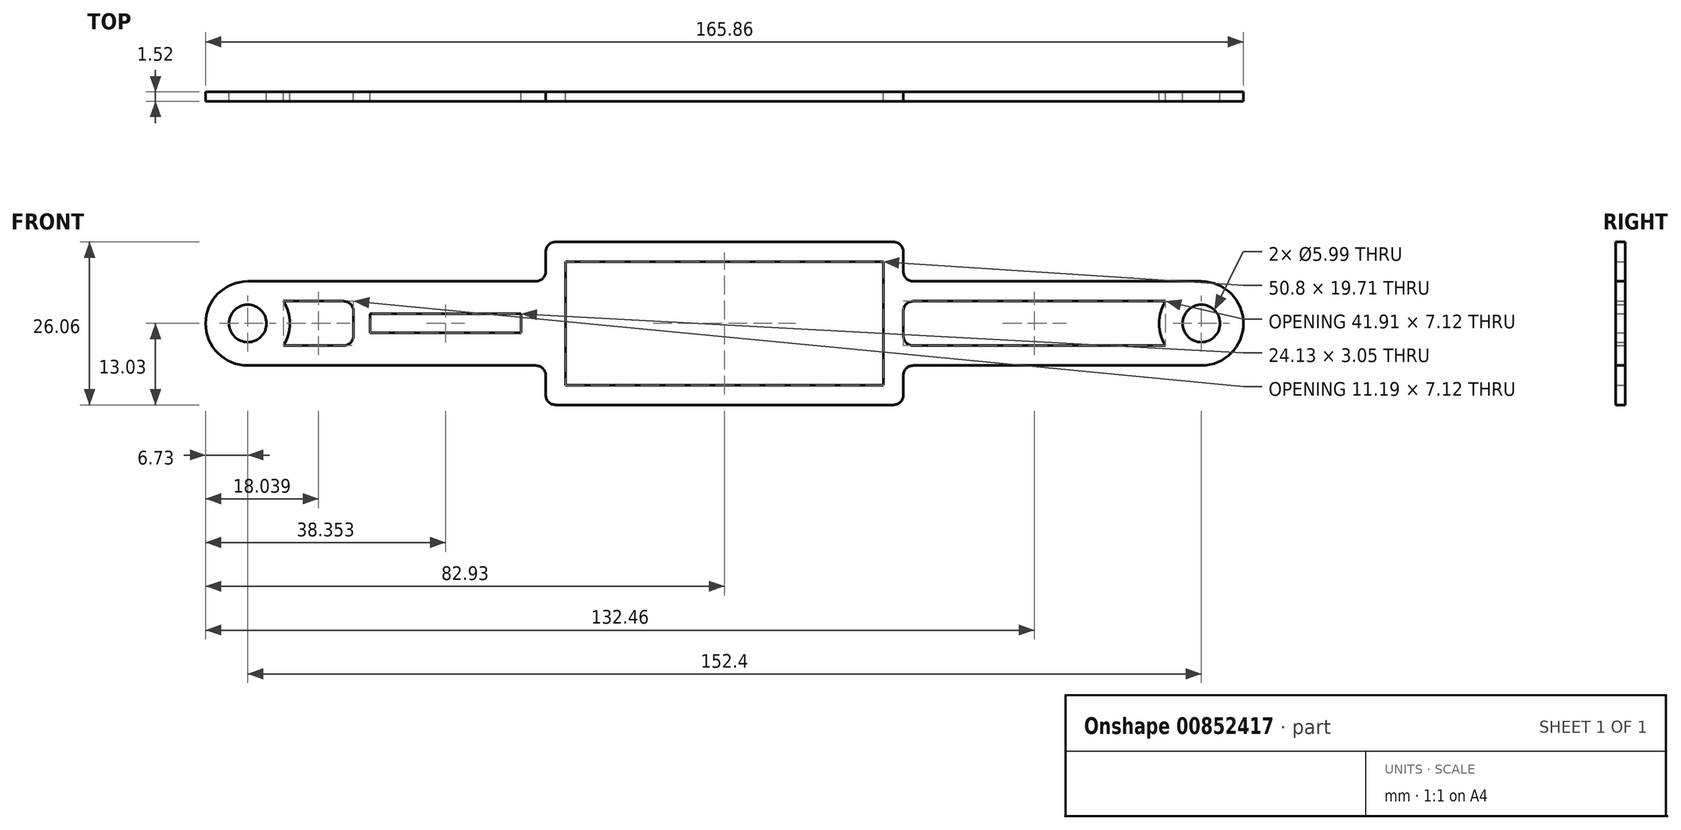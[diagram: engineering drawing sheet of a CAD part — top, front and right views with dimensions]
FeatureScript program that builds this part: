
annotation { "Feature Type Name" : "Feature", "Feature Type Description" : "" }
export const myFeature = defineFeature(function(context is Context, id is Id, definition is map)
    precondition{}
    {
        {
            var Q0;
            Q0=qCreatedBy(makeId("Front.planeOp"),FACE);
            var sketch = newSketch(context, id + "F0", { "sketchPlane" : qUnion([Q0])});
            skLineSegment(sketch, "E0.bottom", {"start": v(-76.2, -6.73) * mm, "end": v(-28.57, -6.73) * mm});
            skLineSegment(sketch, "E0.top", {"start": v(-76.2, 6.73) * mm, "end": v(-28.58, 6.73) * mm});
            skLineSegment(sketch, "E1.bottom", {"start": v(-25.4, 9.86) * mm, "end": v(25.4, 9.86) * mm});
            skLineSegment(sketch, "E1.top", {"start": v(-25.4, -9.86) * mm, "end": v(25.4, -9.86) * mm});
            skLineSegment(sketch, "E1.left", {"start": v(-25.4, 9.86) * mm, "end": v(-25.4, -9.86) * mm});
            skLineSegment(sketch, "E1.right", {"start": v(25.4, 9.86) * mm, "end": v(25.4, -9.86) * mm});
            skCircle(sketch, "E2", {"center": v(-76.2, 0) * mm, "radius": 3 * mm});
            skPoint(sketch, "E2.centerSnap0", {"position": v(-88.9, 0) * mm});
            skCircle(sketch, "E3", {"center": v(76.2, 0) * mm, "radius": 3 * mm});
            skLineSegment(sketch, "E4.bottom", {"start": v(-28.58, 13.03) * mm, "end": v(28.58, 13.03) * mm});
            skLineSegment(sketch, "E4.top", {"start": v(-28.58, -13.03) * mm, "end": v(28.58, -13.03) * mm});
            skLineSegment(sketch, "E4.left", {"start": v(-28.58, 13.03) * mm, "end": v(-28.58, 6.73) * mm});
            skLineSegment(sketch, "E4.right", {"start": v(28.58, 13.03) * mm, "end": v(28.58, 6.73) * mm});
            skArc(sketch, "E5", {"start": v(76.2, -6.73) * mm, "mid": v(82.93, 0) * mm, "end": v(76.2, 6.73) * mm});
            skArc(sketch, "E6", {"start": v(-76.2, 6.73) * mm, "mid": v(-82.93, 0) * mm, "end": v(-76.2, -6.73) * mm});
            skPoint(sketch, "E7.orphan", {"position": v(-88.9, 6.73) * mm});
            skPoint(sketch, "E8.orphan", {"position": v(-88.9, -6.73) * mm});
            skLineSegment(sketch, "E9.trimOffspring", {"start": v(-28.58, -6.73) * mm, "end": v(-28.58, -13.03) * mm});
            skLineSegment(sketch, "E10.trimOffspring", {"start": v(28.58, -6.73) * mm, "end": v(28.58, -13.03) * mm});
            skLineSegment(sketch, "E11.trimOffspring", {"start": v(28.58, 6.73) * mm, "end": v(76.2, 6.73) * mm});
            skLineSegment(sketch, "E12.trimOffspring", {"start": v(28.58, -6.73) * mm, "end": v(76.2, -6.73) * mm});
            skLineSegment(sketch, "E13.bottom", {"start": v(-70.48, 3.56) * mm, "end": v(-59.3, 3.56) * mm});
            skLineSegment(sketch, "E13.top", {"start": v(-70.48, -3.56) * mm, "end": v(-59.3, -3.56) * mm});
            skLineSegment(sketch, "E13.right", {"start": v(-32.51, 1.52) * mm, "end": v(-32.51, -1.52) * mm});
            skLineSegment(sketch, "E14.bottom", {"start": v(28.58, 3.56) * mm, "end": v(70.48, 3.56) * mm});
            skLineSegment(sketch, "E14.top", {"start": v(28.58, -3.56) * mm, "end": v(70.48, -3.56) * mm});
            skLineSegment(sketch, "E14.left", {"start": v(28.58, 3.56) * mm, "end": v(28.58, -3.56) * mm});
            skArc(sketch, "E15", {"start": v(70.48, 3.56) * mm, "mid": v(69.47, 0) * mm, "end": v(70.48, -3.56) * mm});
            skArc(sketch, "E16.trimOffspring", {"start": v(-70.48, -3.56) * mm, "mid": v(-69.47, 0) * mm, "end": v(-70.48, 3.56) * mm});
            skLineSegment(sketch, "E17", {"start": v(-56.64, 1.52) * mm, "end": v(-56.64, -1.52) * mm});
            skLineSegment(sketch, "E18", {"start": v(-59.3, 3.56) * mm, "end": v(-59.3, -3.56) * mm});
            skLineSegment(sketch, "E19.trimOffspring", {"start": v(-56.64, 1.52) * mm, "end": v(-32.51, 1.52) * mm});
            skLineSegment(sketch, "E20.trimOffspring", {"start": v(-56.64, -1.52) * mm, "end": v(-32.51, -1.52) * mm});
            skPoint(sketch, "E21.end.orphan", {"position": v(-32.51, 0) * mm});
            skSolve(sketch);
        }
        {
            var Q0;
            Q0=makeQuery(id+"F0.imprint","IMPRINT",FACE,{"disambiguationData":[TD([[makeQuery(id+"F0.imprint","IMPRINT",EDGE,{"derivedFrom":sQuery(id+"F0.wireOp",EDGE,"E0.bottom")}),1.0]])]});
            extrude(context, id + "F1", {"entities" : qUnion([Q0]), "depth" : 1.52 * mm, "offsetDistance" : 25.4 * mm});
        }
        {
            var Q0;
            Q0=makeQuery(id+"F1.opExtrude","SWEPT_EDGE",EDGE,{"disambiguationData":[OSD([sQuery(id+"F0.wireOp",EDGE,"E4.bottom"),sQuery(id+"F0.wireOp",EDGE,"E4.left")])]});
            var Q1;
            Q1=makeQuery(id+"F1.opExtrude","SWEPT_EDGE",EDGE,{"disambiguationData":[OSD([sQuery(id+"F0.wireOp",EDGE,"E4.bottom"),sQuery(id+"F0.wireOp",EDGE,"E4.right")])]});
            var Q2;
            Q2=makeQuery(id+"F1.opExtrude","SWEPT_EDGE",EDGE,{"disambiguationData":[OSD([sQuery(id+"F0.wireOp",EDGE,"E4.top"),sQuery(id+"F0.wireOp",EDGE,"E10.trimOffspring")])]});
            var Q3;
            Q3=makeQuery(id+"F1.opExtrude","SWEPT_EDGE",EDGE,{"disambiguationData":[OSD([sQuery(id+"F0.wireOp",EDGE,"E4.top"),sQuery(id+"F0.wireOp",EDGE,"E9.trimOffspring")])]});
            var Q4;
            Q4=makeQuery(id+"F1.opExtrude","SWEPT_EDGE",EDGE,{"disambiguationData":[OSD([sQuery(id+"F0.wireOp",EDGE,"E0.bottom"),sQuery(id+"F0.wireOp",EDGE,"E9.trimOffspring")])]});
            var Q5;
            Q5=makeQuery(id+"F1.opExtrude","SWEPT_EDGE",EDGE,{"disambiguationData":[OSD([sQuery(id+"F0.wireOp",EDGE,"E0.top"),sQuery(id+"F0.wireOp",EDGE,"E4.left")])]});
            var Q6;
            Q6=makeQuery(id+"F1.opExtrude","SWEPT_EDGE",EDGE,{"disambiguationData":[OSD([sQuery(id+"F0.wireOp",EDGE,"E4.right"),sQuery(id+"F0.wireOp",EDGE,"E11.trimOffspring")])]});
            var Q7;
            Q7=makeQuery(id+"F1.opExtrude","SWEPT_EDGE",EDGE,{"disambiguationData":[OSD([sQuery(id+"F0.wireOp",EDGE,"E14.bottom"),sQuery(id+"F0.wireOp",EDGE,"E14.left")])]});
            var Q8;
            Q8=makeQuery(id+"F1.opExtrude","SWEPT_EDGE",EDGE,{"disambiguationData":[OSD([sQuery(id+"F0.wireOp",EDGE,"E10.trimOffspring"),sQuery(id+"F0.wireOp",EDGE,"E12.trimOffspring")])]});
            var Q9;
            Q9=makeQuery(id+"F1.opExtrude","SWEPT_EDGE",EDGE,{"disambiguationData":[OSD([sQuery(id+"F0.wireOp",EDGE,"E14.top"),sQuery(id+"F0.wireOp",EDGE,"E14.left")])]});
            var Q10;
            Q10=makeQuery(id+"F1.opExtrude","SWEPT_EDGE",EDGE,{"disambiguationData":[OSD([sQuery(id+"F0.wireOp",EDGE,"E13.bottom"),sQuery(id+"F0.wireOp",EDGE,"E18")])]});
            var Q11;
            Q11=makeQuery(id+"F1.opExtrude","SWEPT_EDGE",EDGE,{"disambiguationData":[OSD([sQuery(id+"F0.wireOp",EDGE,"E13.top"),sQuery(id+"F0.wireOp",EDGE,"E18")])]});
            fillet(context, id + "F2", {"entities" : qUnion([Q0, Q1, Q2, Q3, Q4, Q5, Q6, Q7, Q8, Q9, Q10, Q11]), "radius" : 1.59 * mm, "tangentPropagation" : true, "allowEdgeOverflow" : false});
        }
    });
